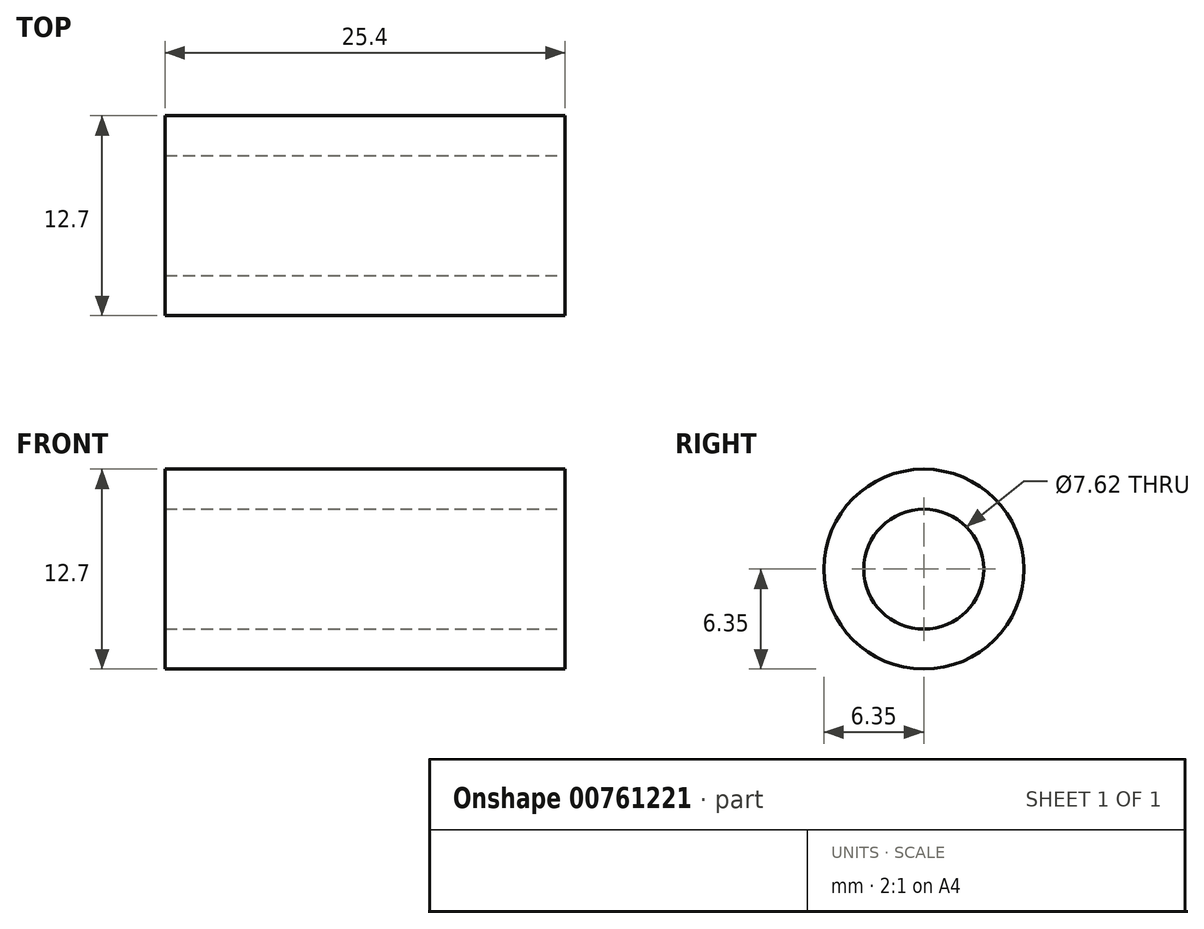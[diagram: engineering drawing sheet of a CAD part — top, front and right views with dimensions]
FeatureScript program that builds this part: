
annotation { "Feature Type Name" : "Feature", "Feature Type Description" : "" }
export const myFeature = defineFeature(function(context is Context, id is Id, definition is map)
    precondition{}
    {
        {
            var Q0;
            Q0=qCreatedBy(makeId("Front.planeOp"),FACE);
            var sketch = newSketch(context, id + "F0", { "sketchPlane" : qUnion([Q0]), "disableImprinting" : false});
            skLineSegment(sketch, "E0", {"start": v(0, 3.8) * mm, "end": v(-25.4, 3.8) * mm});
            skLineSegment(sketch, "E1", {"start": v(-25.4, 3.8) * mm, "end": v(-25.4, 6.35) * mm});
            skLineSegment(sketch, "E2", {"start": v(-25.4, 6.35) * mm, "end": v(0, 6.35) * mm});
            skLineSegment(sketch, "E3", {"start": v(0, 6.35) * mm, "end": v(0, 3.8) * mm});
            skLineSegment(sketch, "E4", {"start": v(0, 0) * mm, "end": v(-25.4, 0) * mm, "construction": true});
            skSolve(sketch);
        }
        {
            var Q0;
            Q0=makeQuery(id+"F0.imprint","IMPRINT",FACE,{"disambiguationData":[TD([[makeQuery(id+"F0.imprint","IMPRINT",EDGE,{"derivedFrom":sQuery(id+"F0.wireOp",EDGE,"E0")}),-1.0]])]});
            var Q1;
            Q1=sQuery(id+"F0.wireOp",EDGE,"E1");
            var Q2;
            Q2=sQuery(id+"F0.wireOp",EDGE,"E2");
            var Q3;
            Q3=sQuery(id+"F0.wireOp",EDGE,"E3");
            var Q4;
            Q4=sQuery(id+"F0.wireOp",EDGE,"E0");
            var Q5;
            Q5=sQuery(id+"F0.wireOp",EDGE,"E4");
            revolve(context, id + "F1", {"surfaceOperationType" : NewSurfaceOperationType.NEW, "entities" : qUnion([Q0]), "surfaceEntities" : qUnion([Q1, Q2, Q3, Q4]), "thickness1" : 5 * mm, "thickness2" : 0 * mm, "thickness" : 5 * mm, "axis" : qUnion([Q5]), "revolveType" : RevolveType.FULL});
        }
    });
